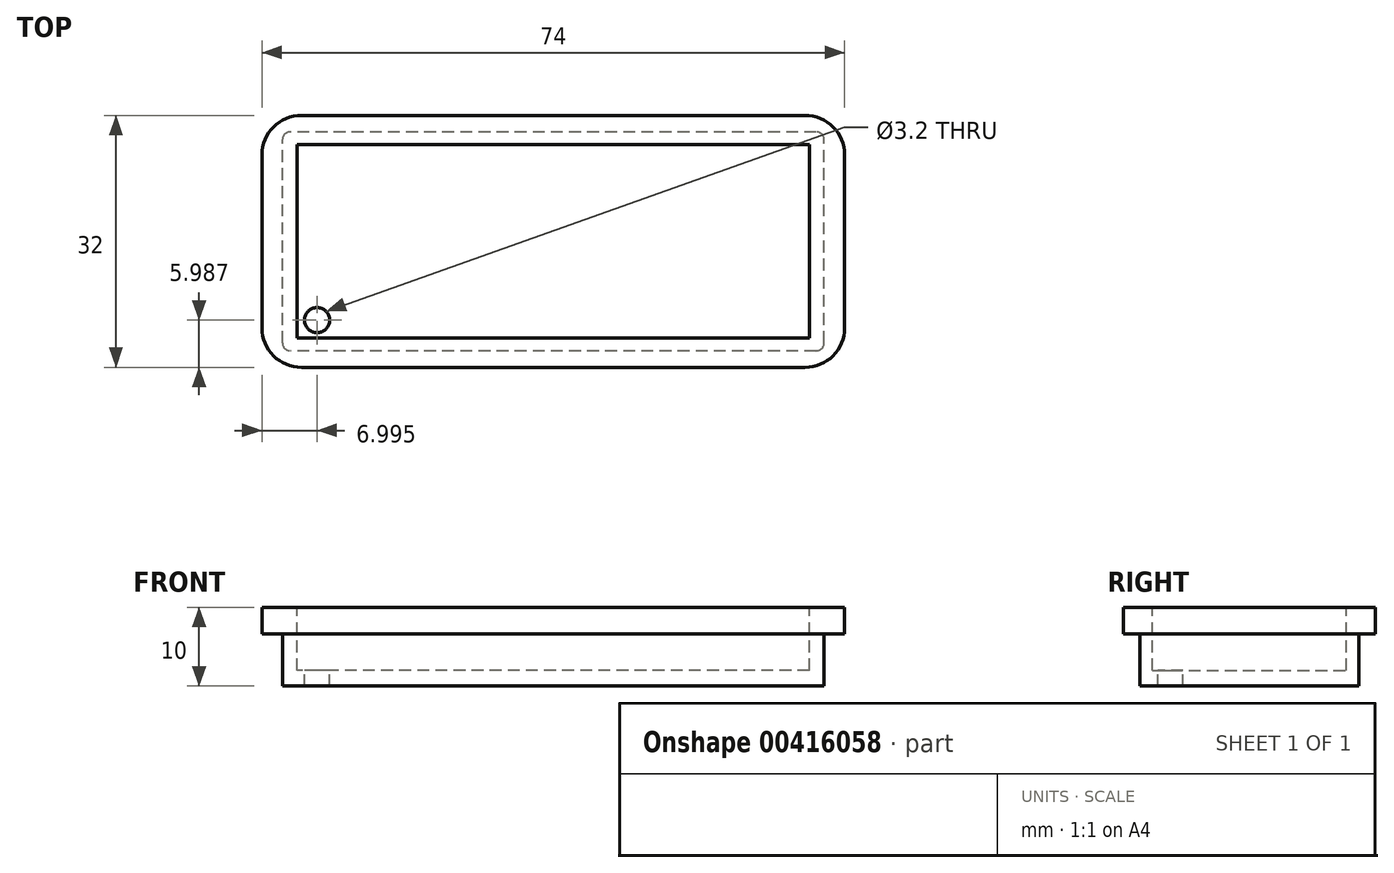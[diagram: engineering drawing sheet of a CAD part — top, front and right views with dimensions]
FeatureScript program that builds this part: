
annotation { "Feature Type Name" : "Feature", "Feature Type Description" : "" }
export const myFeature = defineFeature(function(context is Context, id is Id, definition is map)
    precondition{}
    {
        {
            var Q0;
            Q0=qCreatedBy(makeId("Top.planeOp"),FACE);
            var sketch = newSketch(context, id + "F0", { "sketchPlane" : qUnion([Q0])});
            skLineSegment(sketch, "E0.bottom", {"start": v(37, -16) * mm, "end": v(-37, -16) * mm});
            skLineSegment(sketch, "E0.top", {"start": v(37, 16) * mm, "end": v(-37, 16) * mm});
            skLineSegment(sketch, "E0.left", {"start": v(37, -16) * mm, "end": v(37, 16) * mm});
            skLineSegment(sketch, "E0.right", {"start": v(-37, -16) * mm, "end": v(-37, 16) * mm});
            skPoint(sketch, "E0.middle", {"position": v(0, 0) * mm});
            skSolve(sketch);
        }
        {
            var Q0;
            Q0 = qSketchRegion(id + "F0", true);
            extrude(context, id + "F1", {"entities" : qUnion([Q0]), "depth" : 3.4 * mm});
        }
        {
            var Q0;
            Q0=makeQuery(id+"F1.opExtrude","CAP_FACE",FACE,{"disambiguationData":[OSD([sQuery(id+"F0.wireOp",EDGE,"E0.bottom"),sQuery(id+"F0.wireOp",EDGE,"E0.top"),sQuery(id+"F0.wireOp",EDGE,"E0.left"),sQuery(id+"F0.wireOp",EDGE,"E0.right")])],"isStart":false});
            var sketch = newSketch(context, id + "F2", { "sketchPlane" : qUnion([Q0])});
            skLineSegment(sketch, "E1.bottom", {"start": v(34.4, -13.9) * mm, "end": v(-34.4, -13.9) * mm});
            skLineSegment(sketch, "E1.top", {"start": v(34.4, 13.9) * mm, "end": v(-34.4, 13.9) * mm});
            skLineSegment(sketch, "E1.left", {"start": v(34.4, -13.9) * mm, "end": v(34.4, 13.9) * mm});
            skLineSegment(sketch, "E1.right", {"start": v(-34.4, -13.9) * mm, "end": v(-34.4, 13.9) * mm});
            skPoint(sketch, "E1.middle", {"position": v(0, 0) * mm});
            skSolve(sketch);
        }
        {
            var Q0;
            Q0 = qSketchRegion(id + "F2", true);
            extrude(context, id + "F3", {"entities" : qUnion([Q0]), "operationType" : NewBodyOperationType.ADD, "oppositeDirection" : true, "depth" : 10 * mm});
        }
        {
            var Q0;
            Q0=makeQuery(id+"F2.imprint","IMPRINT",FACE,{"disambiguationData":[TD([[makeQuery(id+"F2.imprint","IMPRINT",EDGE,{"derivedFrom":sQuery(id+"F2.wireOp",EDGE,"E1.bottom")}),-1.0]])]});
            var sketch = newSketch(context, id + "F4", { "sketchPlane" : qUnion([Q0])});
            skLineSegment(sketch, "E2.bottom", {"start": v(32.53, -12.3) * mm, "end": v(-32.53, -12.3) * mm});
            skLineSegment(sketch, "E2.top", {"start": v(32.53, 12.3) * mm, "end": v(-32.53, 12.3) * mm});
            skLineSegment(sketch, "E2.left", {"start": v(32.53, -12.3) * mm, "end": v(32.53, 12.3) * mm});
            skLineSegment(sketch, "E2.right", {"start": v(-32.53, -12.3) * mm, "end": v(-32.53, 12.3) * mm});
            skPoint(sketch, "E2.middle", {"position": v(0, 0) * mm});
            skSolve(sketch);
        }
        {
            var Q0;
            Q0 = qSketchRegion(id + "F4", true);
            extrude(context, id + "F5", {"entities" : qUnion([Q0]), "operationType" : NewBodyOperationType.REMOVE, "oppositeDirection" : true, "depth" : 8 * mm});
        }
        {
            var Q0;
            Q0=makeQuery(id+"F1.opExtrude","SWEPT_EDGE",EDGE,{"disambiguationData":[OSD([sQuery(id+"F0.wireOp",EDGE,"E0.bottom"),sQuery(id+"F0.wireOp",EDGE,"E0.right")])]});
            var Q1;
            Q1=makeQuery(id+"F1.opExtrude","SWEPT_EDGE",EDGE,{"disambiguationData":[OSD([sQuery(id+"F0.wireOp",EDGE,"E0.bottom"),sQuery(id+"F0.wireOp",EDGE,"E0.left")])]});
            var Q2;
            Q2=makeQuery(id+"F1.opExtrude","SWEPT_EDGE",EDGE,{"disambiguationData":[OSD([sQuery(id+"F0.wireOp",EDGE,"E0.top"),sQuery(id+"F0.wireOp",EDGE,"E0.left")])]});
            var Q3;
            Q3=makeQuery(id+"F1.opExtrude","SWEPT_EDGE",EDGE,{"disambiguationData":[OSD([sQuery(id+"F0.wireOp",EDGE,"E0.top"),sQuery(id+"F0.wireOp",EDGE,"E0.right")])]});
            fillet(context, id + "F6", {"entities" : qUnion([Q0, Q1, Q2, Q3]), "radius" : 5 * mm, "tangentPropagation" : true, "allowEdgeOverflow" : false});
        }
        {
            var Q0;
            Q0=makeQuery(id+"F2.imprint","IMPRINT",FACE,{"disambiguationData":[TD([[makeQuery(id+"F2.imprint","IMPRINT",EDGE,{"derivedFrom":sQuery(id+"F2.wireOp",EDGE,"E1.bottom")}),-1.0]])]});
            var sketch = newSketch(context, id + "F7", { "sketchPlane" : qUnion([Q0])});
            skCircle(sketch, "E3", {"center": v(-30, -10.01) * mm, "radius": 1.6 * mm});
            skSolve(sketch);
        }
        {
            var Q0;
            Q0 = qSketchRegion(id + "F7", true);
            extrude(context, id + "F8", {"entities" : qUnion([Q0]), "operationType" : NewBodyOperationType.REMOVE, "endBound" : BoundingType.THROUGH_ALL, "oppositeDirection" : true, "depth" : 25 * mm});
        }
        {
            var Q0;
            Q0=makeQuery(id+"F3.opExtrude","SWEPT_EDGE",EDGE,{"disambiguationData":[OSD([sQuery(id+"F2.wireOp",EDGE,"E1.top"),sQuery(id+"F2.wireOp",EDGE,"E1.right")])]});
            var Q1;
            Q1=makeQuery(id+"F3.opExtrude","SWEPT_EDGE",EDGE,{"disambiguationData":[OSD([sQuery(id+"F2.wireOp",EDGE,"E1.bottom"),sQuery(id+"F2.wireOp",EDGE,"E1.right")])]});
            var Q2;
            Q2=makeQuery(id+"F3.opExtrude","SWEPT_EDGE",EDGE,{"disambiguationData":[OSD([sQuery(id+"F2.wireOp",EDGE,"E1.bottom"),sQuery(id+"F2.wireOp",EDGE,"E1.left")])]});
            var Q3;
            Q3=makeQuery(id+"F3.opExtrude","SWEPT_EDGE",EDGE,{"disambiguationData":[OSD([sQuery(id+"F2.wireOp",EDGE,"E1.top"),sQuery(id+"F2.wireOp",EDGE,"E1.left")])]});
            fillet(context, id + "F9", {"entities" : qUnion([Q0, Q1, Q2, Q3]), "radius" : 1 * mm, "tangentPropagation" : true, "allowEdgeOverflow" : false});
        }
    });
